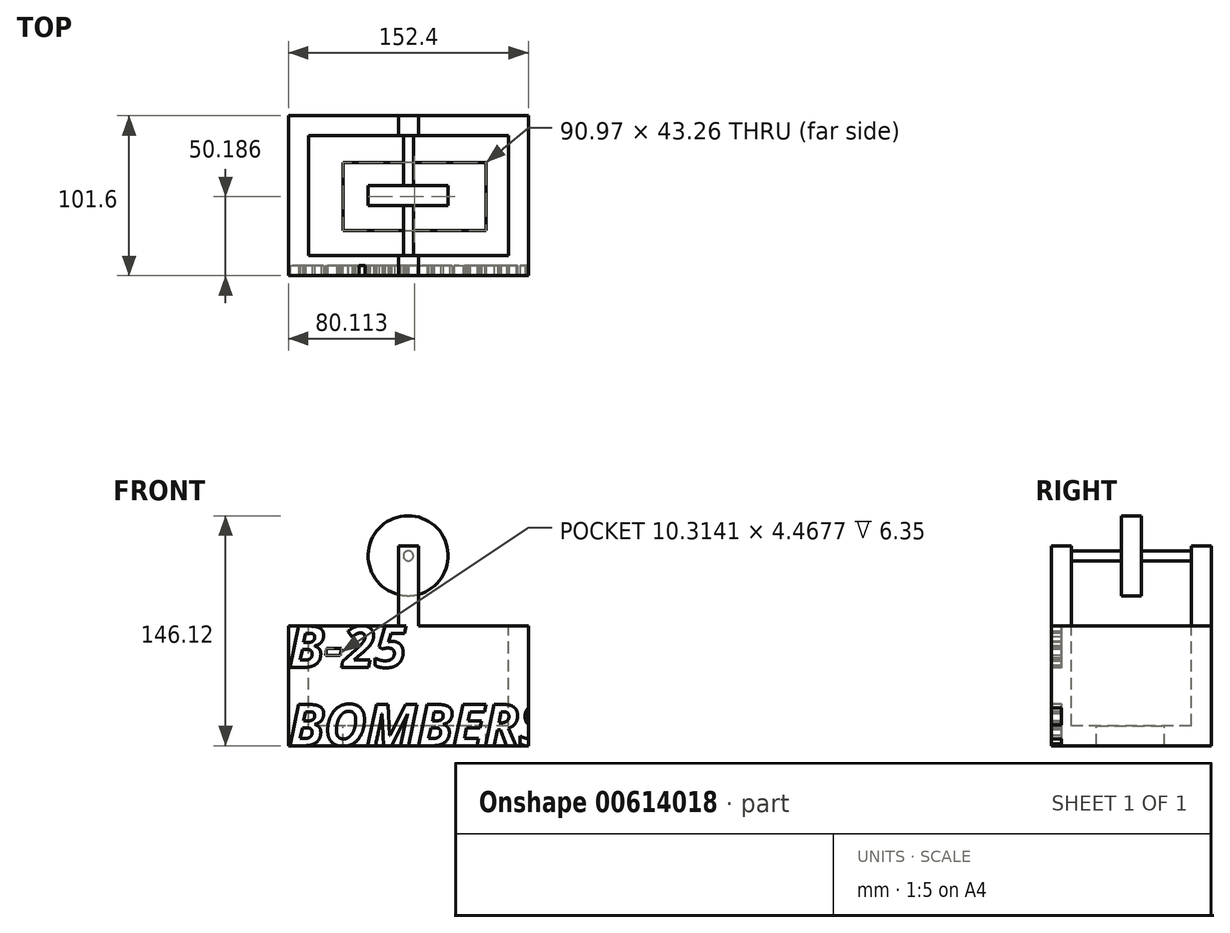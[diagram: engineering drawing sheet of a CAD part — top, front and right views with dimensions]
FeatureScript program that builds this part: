
annotation { "Feature Type Name" : "Feature", "Feature Type Description" : "" }
export const myFeature = defineFeature(function(context is Context, id is Id, definition is map)
    precondition{}
    {
        {
            var Q0;
            Q0=qCreatedBy(makeId("Front.planeOp"),FACE);
            var sketch = newSketch(context, id + "F0", { "sketchPlane" : qUnion([Q0])});
            skLineSegment(sketch, "E0.bottom", {"start": v(-79.88, 24.12) * mm, "end": v(72.52, 24.12) * mm});
            skLineSegment(sketch, "E0.top", {"start": v(-79.88, -52.08) * mm, "end": v(72.52, -52.08) * mm});
            skLineSegment(sketch, "E0.left", {"start": v(-79.88, 24.12) * mm, "end": v(-79.88, -52.08) * mm});
            skLineSegment(sketch, "E0.right", {"start": v(72.52, 24.12) * mm, "end": v(72.52, -52.08) * mm});
            skSolve(sketch);
        }
        {
            var Q0;
            Q0 = qSketchRegion(id + "F0", true);
            extrude(context, id + "F1", {"entities" : qUnion([Q0]), "oppositeDirection" : true, "depth" : 101.6 * mm, "offsetDistance" : 25.4 * mm});
        }
        {
            var Q0;
            Q0=makeQuery(id+"F1.opExtrude","SWEPT_FACE",FACE,{"disambiguationData":[OSD([sQuery(id+"F0.wireOp",EDGE,"E0.bottom")])]});
            var sketch = newSketch(context, id + "F2", { "sketchPlane" : qUnion([Q0])});
            skLineSegment(sketch, "E1", {"start": v(-67.18, 88.9) * mm, "end": v(-67.18, 12.7) * mm});
            skLineSegment(sketch, "E2", {"start": v(-67.18, 12.7) * mm, "end": v(59.82, 12.7) * mm});
            skLineSegment(sketch, "E3", {"start": v(59.82, 12.7) * mm, "end": v(59.82, 88.9) * mm});
            skLineSegment(sketch, "E4", {"start": v(59.82, 88.9) * mm, "end": v(-67.18, 88.9) * mm});
            skSolve(sketch);
        }
        {
            var Q0;
            Q0=makeQuery(id+"F2.imprint","IMPRINT",FACE,{"disambiguationData":[TD([[makeQuery(id+"F2.imprint","IMPRINT",EDGE,{"derivedFrom":sQuery(id+"F2.wireOp",EDGE,"E1")}),1.0]])]});
            extrude(context, id + "F3", {"entities" : qUnion([Q0]), "operationType" : NewBodyOperationType.REMOVE, "oppositeDirection" : true, "depth" : 63.5 * mm, "offsetDistance" : 25.4 * mm});
        }
        {
            var Q0;
            Q0=makeQuery(id+"F3.boolean.opBoolean","COPY",FACE,{"derivedFrom":makeQuery(id+"F3.opExtrude","CAP_FACE",FACE,{"disambiguationData":[OSD([sQuery(id+"F2.wireOp",EDGE,"E1"),sQuery(id+"F2.wireOp",EDGE,"E2"),sQuery(id+"F2.wireOp",EDGE,"E3"),sQuery(id+"F2.wireOp",EDGE,"E4")])],"isStart":false})});
            var sketch = newSketch(context, id + "F4", { "sketchPlane" : qUnion([Q0])});
            skLineSegment(sketch, "E5", {"start": v(-45.25, 71.82) * mm, "end": v(-45.25, 28.55) * mm});
            skLineSegment(sketch, "E6", {"start": v(-45.25, 28.55) * mm, "end": v(45.72, 28.55) * mm});
            skLineSegment(sketch, "E7", {"start": v(45.72, 28.55) * mm, "end": v(45.72, 71.82) * mm});
            skLineSegment(sketch, "E8", {"start": v(45.72, 71.82) * mm, "end": v(-45.25, 71.82) * mm});
            skSolve(sketch);
        }
        {
            var Q0;
            Q0=makeQuery(id+"F4.imprint","IMPRINT",FACE,{"disambiguationData":[TD([[makeQuery(id+"F4.imprint","IMPRINT",EDGE,{"derivedFrom":sQuery(id+"F4.wireOp",EDGE,"E5")}),1.0]])]});
            extrude(context, id + "F5", {"entities" : qUnion([Q0]), "operationType" : NewBodyOperationType.REMOVE, "oppositeDirection" : true, "depth" : 127 * mm, "offsetDistance" : 25.4 * mm});
        }
        {
            var Q0;
            Q0=makeQuery(id+"F1.opExtrude","SWEPT_FACE",FACE,{"disambiguationData":[OSD([sQuery(id+"F0.wireOp",EDGE,"E0.bottom")])]});
            var sketch = newSketch(context, id + "F6", { "sketchPlane" : qUnion([Q0])});
            skLineSegment(sketch, "E9", {"start": v(-10.03, 101.6) * mm, "end": v(-10.03, 88.9) * mm});
            skLineSegment(sketch, "E10", {"start": v(-10.03, 88.9) * mm, "end": v(2.67, 88.9) * mm});
            skLineSegment(sketch, "E11", {"start": v(2.67, 88.9) * mm, "end": v(2.67, 101.6) * mm});
            skLineSegment(sketch, "E12", {"start": v(2.67, 101.6) * mm, "end": v(-10.03, 101.6) * mm});
            skLineSegment(sketch, "E13", {"start": v(2.67, 0) * mm, "end": v(2.67, 12.7) * mm});
            skLineSegment(sketch, "E14", {"start": v(2.67, 12.7) * mm, "end": v(-10.03, 12.7) * mm});
            skLineSegment(sketch, "E15", {"start": v(-10.03, 12.7) * mm, "end": v(-10.03, 0) * mm});
            skLineSegment(sketch, "E16", {"start": v(-10.03, 0) * mm, "end": v(2.67, 0) * mm});
            skSolve(sketch);
        }
        {
            var Q0;
            Q0 = qSketchRegion(id + "F6", true);
            extrude(context, id + "F7", {"entities" : qUnion([Q0]), "operationType" : NewBodyOperationType.ADD, "depth" : 50.8 * mm, "offsetDistance" : 25.4 * mm});
        }
        {
            var Q0;
            Q0=makeQuery(id+"F7.boolean.opBoolean","MERGE",FACE,{"derivedFrom":[makeQuery(id+"F1.opExtrude","CAP_FACE",FACE,{"disambiguationData":[OSD([sQuery(id+"F0.wireOp",EDGE,"E0.bottom"),sQuery(id+"F0.wireOp",EDGE,"E0.top"),sQuery(id+"F0.wireOp",EDGE,"E0.left"),sQuery(id+"F0.wireOp",EDGE,"E0.right")])],"isStart":false}),makeQuery(id+"F7.opExtrude","SWEPT_FACE",FACE,{"disambiguationData":[OSD([sQuery(id+"F6.wireOp",EDGE,"E12")])]})]});
            var sketch = newSketch(context, id + "F8", { "sketchPlane" : qUnion([Q0])});
            skCircle(sketch, "E17", {"center": v(3.68, 68.57) * mm, "radius": 3.18 * mm});
            skSolve(sketch);
        }
        {
            var Q0;
            Q0=makeQuery(id+"F8.imprint","IMPRINT",FACE,{"disambiguationData":[TD([[makeQuery(id+"F8.imprint","IMPRINT",EDGE,{"derivedFrom":sQuery(id+"F8.wireOp",EDGE,"E17")}),1.0]])]});
            extrude(context, id + "F9", {"entities" : qUnion([Q0]), "operationType" : NewBodyOperationType.ADD, "oppositeDirection" : true, "depth" : 101.6 * mm, "offsetDistance" : 25.4 * mm});
        }
        {
            var Q0;
            Q0=qCreatedBy(makeId("Front.planeOp"),FACE);
            cPlane(context, id + "F10", {"entities" : qUnion([Q0]), "cplaneType" : CPlaneType.OFFSET, "offset" : 50.8 * mm, "oppositeDirection" : true, "width" : 152.4 * mm, "height" : 152.4 * mm});
        }
        {
            var Q0;
            Q0=qCreatedBy(id+"F10.planeOp",FACE);
            var sketch = newSketch(context, id + "F11", { "sketchPlane" : qUnion([Q0])});
            skCircle(sketch, "E18", {"center": v(-3.83, 68.64) * mm, "radius": 25.4 * mm});
            skSolve(sketch);
        }
        {
            var Q0;
            Q0=makeQuery(id+"F11.imprint","IMPRINT",FACE,{"disambiguationData":[TD([[makeQuery(id+"F11.imprint","IMPRINT",EDGE,{"derivedFrom":sQuery(id+"F11.wireOp",EDGE,"E18")}),1.0]])]});
            extrude(context, id + "F12", {"entities" : qUnion([Q0]), "operationType" : NewBodyOperationType.ADD, "endBound" : BoundingType.SYMMETRIC, "depth" : 12.7 * mm, "offsetDistance" : 25.4 * mm});
        }
        {
            var Q0;
            Q0=makeQuery(id+"F7.boolean.opBoolean","MERGE",FACE,{"derivedFrom":[makeQuery(id+"F3.boolean.opBoolean","COPY",FACE,{"derivedFrom":makeQuery(id+"F3.opExtrude","SWEPT_FACE",FACE,{"disambiguationData":[OSD([sQuery(id+"F2.wireOp",EDGE,"E4")])]})}),makeQuery(id+"F7.opExtrude","SWEPT_FACE",FACE,{"disambiguationData":[OSD([sQuery(id+"F6.wireOp",EDGE,"E10")])]})]});
            var sketch = newSketch(context, id + "F13", { "sketchPlane" : qUnion([Q0])});
            skCircle(sketch, "E19", {"center": v(49.86, -33.03) * mm, "radius": 6.35 * mm});
            skSolve(sketch);
        }
        {
            var Q0;
            Q0=sQuery(id+"F13.wireOp",EDGE,"E19");
            extrude(context, id + "F14", {"bodyType" : ToolBodyType.SURFACE, "surfaceEntities" : qUnion([Q0]), "depth" : 76.2 * mm, "offsetDistance" : 25.4 * mm});
        }
        {
            var Q0;
            Q0=makeQuery(id+"F7.boolean.opBoolean","MERGE",FACE,{"derivedFrom":[makeQuery(id+"F1.opExtrude","CAP_FACE",FACE,{"disambiguationData":[OSD([sQuery(id+"F0.wireOp",EDGE,"E0.bottom"),sQuery(id+"F0.wireOp",EDGE,"E0.top"),sQuery(id+"F0.wireOp",EDGE,"E0.left"),sQuery(id+"F0.wireOp",EDGE,"E0.right")])],"isStart":true}),makeQuery(id+"F7.opExtrude","SWEPT_FACE",FACE,{"disambiguationData":[OSD([sQuery(id+"F6.wireOp",EDGE,"E16")])]})]});
            var sketch = newSketch(context, id + "F15", { "sketchPlane" : qUnion([Q0])});
            skText(sketch, "E20", { "text": "B-25\nBOMBERS\n", "fontName": "OpenSans-BoldItalic.ttf"});
            const initialGuessF15  = {"E20": [-0.07988, -0.00223, 1, 0, 0.02636]};
            skSetInitialGuess(sketch, initialGuessF15);
            skSolve(sketch);
        }
        {
            var Q0;
            Q0 = qSketchRegion(id + "F15", true);
            extrude(context, id + "F16", {"entities" : qUnion([Q0]), "operationType" : NewBodyOperationType.REMOVE, "oppositeDirection" : true, "depth" : 6.35 * mm, "offsetDistance" : 25.4 * mm});
        }
    });
